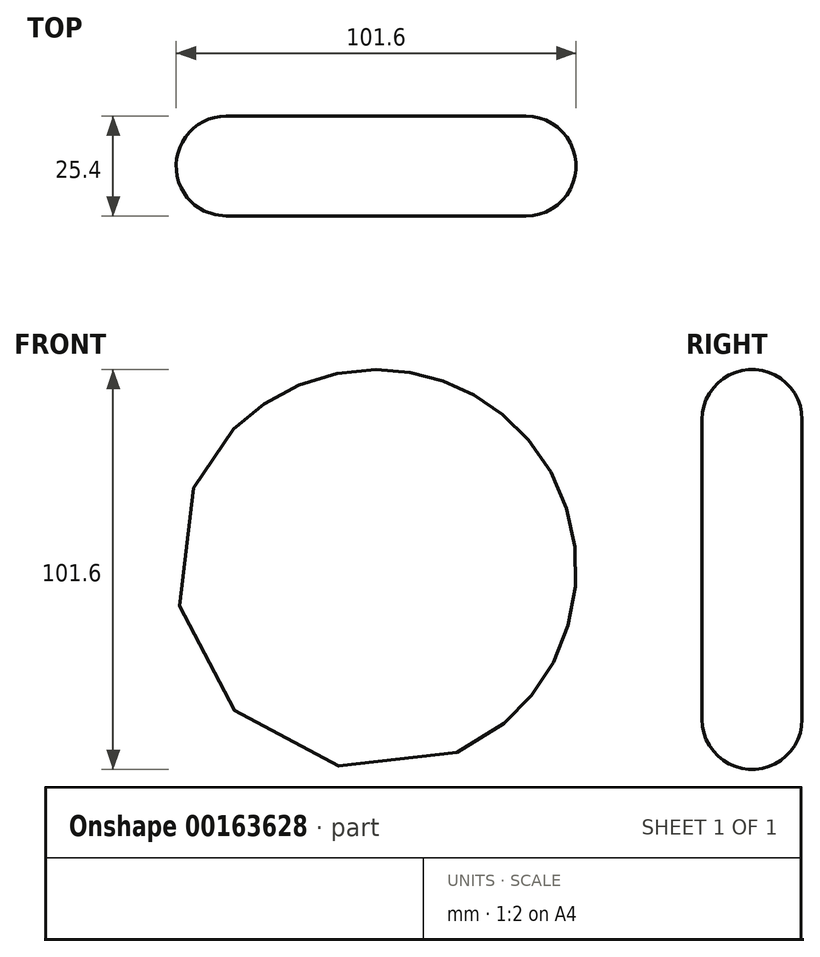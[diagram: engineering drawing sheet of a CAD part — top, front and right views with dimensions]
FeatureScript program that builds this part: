
annotation { "Feature Type Name" : "Feature", "Feature Type Description" : "" }
export const myFeature = defineFeature(function(context is Context, id is Id, definition is map)
    precondition{}
    {
        {
            var Q0;
            Q0=qCreatedBy(makeId("Right.planeOp"),FACE);
            var sketch = newSketch(context, id + "F0", { "sketchPlane" : qUnion([Q0])});
            skLineSegment(sketch, "E0.bottom", {"start": v(0, 0) * mm, "end": v(12.7, 0) * mm});
            skLineSegment(sketch, "E0.top", {"start": v(0, 50.8) * mm, "end": v(0, 50.8) * mm});
            skLineSegment(sketch, "E0.left", {"start": v(0, 0) * mm, "end": v(0, 50.8) * mm});
            skLineSegment(sketch, "E0.right", {"start": v(12.7, 0) * mm, "end": v(12.7, 38.1) * mm});
            skPoint(sketch, "E1.visualSharp", {"position": v(12.7, 50.8) * mm});
            skArc(sketch, "E1.filletArc", {"start": v(12.7, 38.1) * mm, "mid": v(8.98, 47.08) * mm, "end": v(0, 50.8) * mm});
            skLineSegment(sketch, "E2", {"start": v(0, 0) * mm, "end": v(29.52, 0) * mm, "construction": true});
            skPoint(sketch, "E2.endSnap0", {"position": v(6.35, 0) * mm});
            skLineSegment(sketch, "E3.MirrorCS", {"start": v(0, 0) * mm, "end": v(-12.7, 0) * mm});
            skLineSegment(sketch, "E4.MirrorCS", {"start": v(-12.7, 0) * mm, "end": v(-12.7, 38.1) * mm});
            skArc(sketch, "E5.MirrorCS", {"start": v(-12.7, 38.1) * mm, "mid": v(-8.98, 47.08) * mm, "end": v(0, 50.8) * mm});
            skLineSegment(sketch, "E6.MirrorCS", {"start": v(0, 0) * mm, "end": v(-29.52, 0) * mm, "construction": true});
            skSolve(sketch);
        }
        {
            var Q0;
            Q0=makeQuery(id+"F0.imprint","IMPRINT",FACE,{"disambiguationData":[TD([[makeQuery(id+"F0.imprint","IMPRINT",EDGE,{"derivedFrom":sQuery(id+"F0.wireOp",EDGE,"E0.left")}),1.0]])]});
            var Q1;
            Q1=makeQuery(id+"F0.imprint","IMPRINT",FACE,{"disambiguationData":[TD([[makeQuery(id+"F0.imprint","IMPRINT",EDGE,{"derivedFrom":sQuery(id+"F0.wireOp",EDGE,"E0.bottom")}),1.0]])]});
            var Q2;
            Q2=sQuery(id+"F0.wireOp",EDGE,"E6.MirrorCS");
            revolve(context, id + "F1", {"entities" : qUnion([Q0, Q1]), "axis" : qUnion([Q2]), "revolveType" : RevolveType.FULL});
        }
    });
